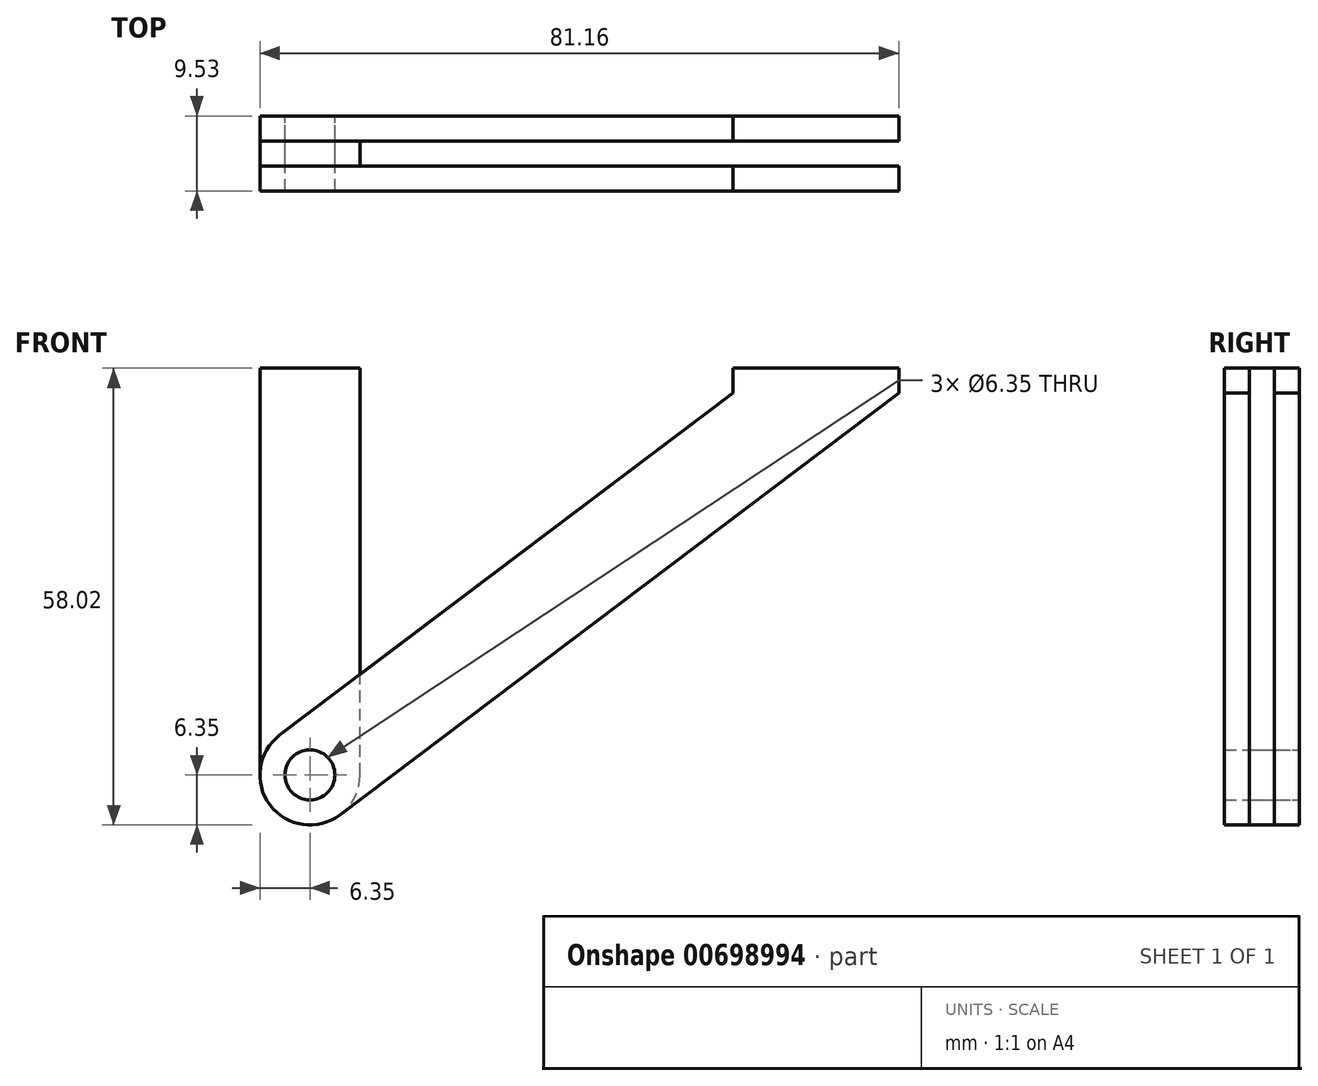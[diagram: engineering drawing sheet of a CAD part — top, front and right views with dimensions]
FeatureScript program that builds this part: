
annotation { "Feature Type Name" : "Feature", "Feature Type Description" : "" }
export const myFeature = defineFeature(function(context is Context, id is Id, definition is map)
    precondition{}
    {
        {
            var Q0;
            Q0=qCreatedBy(makeId("Front.planeOp"),FACE);
            var sketch = newSketch(context, id + "F0", { "sketchPlane" : qUnion([Q0])});
            skLineSegment(sketch, "E0.bottom", {"start": v(0, 0) * mm, "end": v(12.7, 0) * mm});
            skLineSegment(sketch, "E0.top", {"start": v(0, 61.2) * mm, "end": v(12.7, 61.2) * mm});
            skLineSegment(sketch, "E0.left", {"start": v(0, 0) * mm, "end": v(0, 61.2) * mm});
            skLineSegment(sketch, "E0.right", {"start": v(12.7, 0) * mm, "end": v(12.7, 61.2) * mm});
            skLineSegment(sketch, "E1", {"start": v(6.35, 0) * mm, "end": v(6.35, 6.35) * mm});
            skCircle(sketch, "E2", {"center": v(6.35, 6.35) * mm, "radius": 3.18 * mm});
            skLineSegment(sketch, "E3", {"start": v(0, 61.2) * mm, "end": v(0, 58.02) * mm});
            skLineSegment(sketch, "E4", {"start": v(0, 58.02) * mm, "end": v(12.7, 58.02) * mm});
            skSolve(sketch);
        }
        {
            var Q0;
            Q0=makeQuery(id+"F0.imprint","IMPRINT",FACE,{"disambiguationData":[TD([[makeQuery(id+"F0.imprint","IMPRINT",EDGE,{"derivedFrom":sQuery(id+"F0.wireOp",EDGE,"E0.bottom")}),1.0]])]});
            extrude(context, id + "F1", {"entities" : qUnion([Q0]), "depth" : 3.17 * mm, "offsetDistance" : 25.4 * mm});
        }
        {
            var Q0;
            Q0=makeQuery(id+"F1.opExtrude","SWEPT_EDGE",EDGE,{"disambiguationData":[OSD([sQuery(id+"F0.wireOp",EDGE,"E0.bottom"),sQuery(id+"F0.wireOp",EDGE,"E0.right")])]});
            var Q1;
            Q1=makeQuery(id+"F1.opExtrude","SWEPT_EDGE",EDGE,{"disambiguationData":[OSD([sQuery(id+"F0.wireOp",EDGE,"E0.bottom"),sQuery(id+"F0.wireOp",EDGE,"E0.left")])]});
            fillet(context, id + "F2", {"entities" : qUnion([Q0, Q1]), "radius" : 6.35 * mm, "tangentPropagation" : true, "allowEdgeOverflow" : false});
        }
        {
            var Q0;
            Q0=qCreatedBy(makeId("Front.planeOp"),FACE);
            cPlane(context, id + "F3", {"entities" : qUnion([Q0]), "cplaneType" : CPlaneType.OFFSET, "offset" : 3.17 * mm, "width" : 152.4 * mm, "height" : 152.4 * mm});
        }
        {
            var Q0;
            Q0=qCreatedBy(id+"F3.planeOp",FACE);
            var sketch = newSketch(context, id + "F4", { "sketchPlane" : qUnion([Q0])});
            skCircle(sketch, "E5.0", {"center": v(6.35, 6.35) * mm, "radius": 3.18 * mm});
            skCircle(sketch, "E6", {"center": v(6.35, 6.35) * mm, "radius": 6.35 * mm});
            skLineSegment(sketch, "E7", {"start": v(60.07, 58.02) * mm, "end": v(60.07, 54.85) * mm});
            skLineSegment(sketch, "E8", {"start": v(60.07, 54.85) * mm, "end": v(2.52, 11.42) * mm});
            skLineSegment(sketch, "E9", {"start": v(2.52, 11.42) * mm, "end": v(10.18, 1.28) * mm});
            skLineSegment(sketch, "E10", {"start": v(60.07, 54.85) * mm, "end": v(81.16, 54.85) * mm});
            skLineSegment(sketch, "E11", {"start": v(10.18, 1.28) * mm, "end": v(81.16, 54.85) * mm});
            skLineSegment(sketch, "E12", {"start": v(81.16, 54.85) * mm, "end": v(81.16, 58.02) * mm});
            skLineSegment(sketch, "E13", {"start": v(60.07, 58.02) * mm, "end": v(81.16, 58.02) * mm});
            skLineSegment(sketch, "E14.0", {"start": v(0, 58.02) * mm, "end": v(12.7, 58.02) * mm});
            skLineSegment(sketch, "E15", {"start": v(12.7, 58.02) * mm, "end": v(97.42, 58.02) * mm});
            skLineSegment(sketch, "E16.0", {"start": v(12.7, 6.35) * mm, "end": v(12.7, 58.02) * mm});
            skSolve(sketch);
        }
        {
            var Q0;
            {var subQ0=sQuery(id+"F4.wireOp",EDGE,"E9");var subQ1=sQuery(id+"F4.wireOp",EDGE,"E5.0");var subQ2=makeQuery(id+"F4.imprint","INTERSECT",VERTEX,{"disambiguationData":[OD(0.0)],"derivedFrom":[subQ1,subQ0]});Q0=makeQuery(id+"F4.imprint","IMPRINT",FACE,{"disambiguationData":[TD([[makeQuery(id+"F4.imprint","IMPRINT",EDGE,{"disambiguationData":[TD([[subQ2,-1.0]])],"derivedFrom":subQ1}),-1.0]])]});}
            var Q1;
            {var subQ0=sQuery(id+"F4.wireOp",EDGE,"E9");var subQ1=sQuery(id+"F4.wireOp",EDGE,"E5.0");var subQ2=makeQuery(id+"F4.imprint","INTERSECT",VERTEX,{"disambiguationData":[OD(0.0)],"derivedFrom":[subQ1,subQ0]});Q1=makeQuery(id+"F4.imprint","IMPRINT",FACE,{"disambiguationData":[TD([[makeQuery(id+"F4.imprint","IMPRINT",EDGE,{"disambiguationData":[TD([[subQ2,1.0]])],"derivedFrom":subQ1}),-1.0]])]});}
            var Q2;
            {var subQ1=sQuery(id+"F4.wireOp",EDGE,"E8");Q2=makeQuery(id+"F4.imprint","IMPRINT",FACE,{"disambiguationData":[TD([[makeQuery(id+"F4.imprint","IMPRINT",EDGE,{"derivedFrom":subQ1}),1.0]])]});}
            var Q3;
            {var subQ3=sQuery(id+"F4.wireOp",EDGE,"E7");Q3=makeQuery(id+"F4.imprint","IMPRINT",FACE,{"disambiguationData":[TD([[makeQuery(id+"F4.imprint","IMPRINT",EDGE,{"derivedFrom":subQ3}),1.0]])]});}
            var Q4;
            {var subQ1=sQuery(id+"F4.wireOp",EDGE,"E10");Q4=makeQuery(id+"F4.imprint","IMPRINT",FACE,{"disambiguationData":[TD([[makeQuery(id+"F4.imprint","IMPRINT",EDGE,{"derivedFrom":subQ1}),-1.0]])]});}
            extrude(context, id + "F5", {"entities" : qUnion([Q0, Q1, Q2, Q3, Q4]), "depth" : 3.17 * mm, "offsetDistance" : 25.4 * mm});
        }
        {
            var Q0;
            Q0=makeQuery(id+"F5.opExtrude","SWEPT_BODY",BODY,{"disambiguationData":[OSD([sQuery(id+"F4.wireOp",EDGE,"E5.0"),sQuery(id+"F4.wireOp",EDGE,"E6"),sQuery(id+"F4.wireOp",EDGE,"E7"),sQuery(id+"F4.wireOp",EDGE,"E8"),sQuery(id+"F4.wireOp",EDGE,"E11"),sQuery(id+"F4.wireOp",EDGE,"E12"),sQuery(id+"F4.wireOp",EDGE,"E13")])]});
            transform(context, id + "F6", {"entities" : qUnion([Q0]), "transformType" : TransformType.TRANSLATION_3D, "dx" : 0 * mm, "dy" : 6.35 * mm, "dz" : 0 * mm, "makeCopy" : true});
        }
        {
            var Q0;
            Q0=makeQuery(id+"F6.opPattern","COPY",FACE,{"derivedFrom":makeQuery(id+"F5.opExtrude","CAP_FACE",FACE,{"disambiguationData":[OSD([sQuery(id+"F4.wireOp",EDGE,"E5.0"),sQuery(id+"F4.wireOp",EDGE,"E6"),sQuery(id+"F4.wireOp",EDGE,"E7"),sQuery(id+"F4.wireOp",EDGE,"E8"),sQuery(id+"F4.wireOp",EDGE,"E11"),sQuery(id+"F4.wireOp",EDGE,"E12"),sQuery(id+"F4.wireOp",EDGE,"E13")])],"isStart":true}),"instanceName":"1"});
            var sketch = newSketch(context, id + "F7", { "sketchPlane" : qUnion([Q0])});
            skCircle(sketch, "E17.0", {"center": v(-6.35, 6.35) * mm, "radius": 3.18 * mm});
            skSolve(sketch);
        }
        {
            var Q0;
            Q0=makeQuery(id+"F7.imprint","IMPRINT",FACE,{"disambiguationData":[TD([[makeQuery(id+"F7.imprint","IMPRINT",EDGE,{"derivedFrom":sQuery(id+"F7.wireOp",EDGE,"E17.0")}),-1.0]])]});
            extrude(context, id + "F8", {"entities" : qUnion([Q0]), "oppositeDirection" : true, "depth" : 9.52 * mm, "offsetDistance" : 25.4 * mm});
        }
    });
